# Revit family: revitupgrade
name_source: partatom
category: Furniture
units: mm (PartAtom-declared; Revit-internal decimal feet)

## family parameters
Always vertical = Yes
Cut with Voids When Loaded = No
Enable Cutting in Views = No
OmniClass Number = 23.40.70.14.64.11
OmniClass Title = Office Furniture
Render Appearance Source = Family Geometry
Room Calculation Point = No
Shared = No
Work Plane-Based = No

## types (1)
- Buoy
    Assembly Code = E2020200
    Bottom Shell = Steelcase - 6527 Merle
    Default Elevation = 0.00 mm
    Description = Designed for today's movers and shakers, Buoy is a seat that’s as active as you are. Choose from six bold colors and a cap that you can personalize.
    Handle = Steelcase - 4799 Platinum Metallic
    Manufacturer = Steelcase
    Release Date = December 2022
    Seat Upholstery = Steelcase - 5G65 Tornado
    Style Number(s) = TSBUOY
    URL = https://www.steelcase.com

## geometry (parser evidence)
native form markers: Sweep x2
no freeform markers — native parametric forms only
